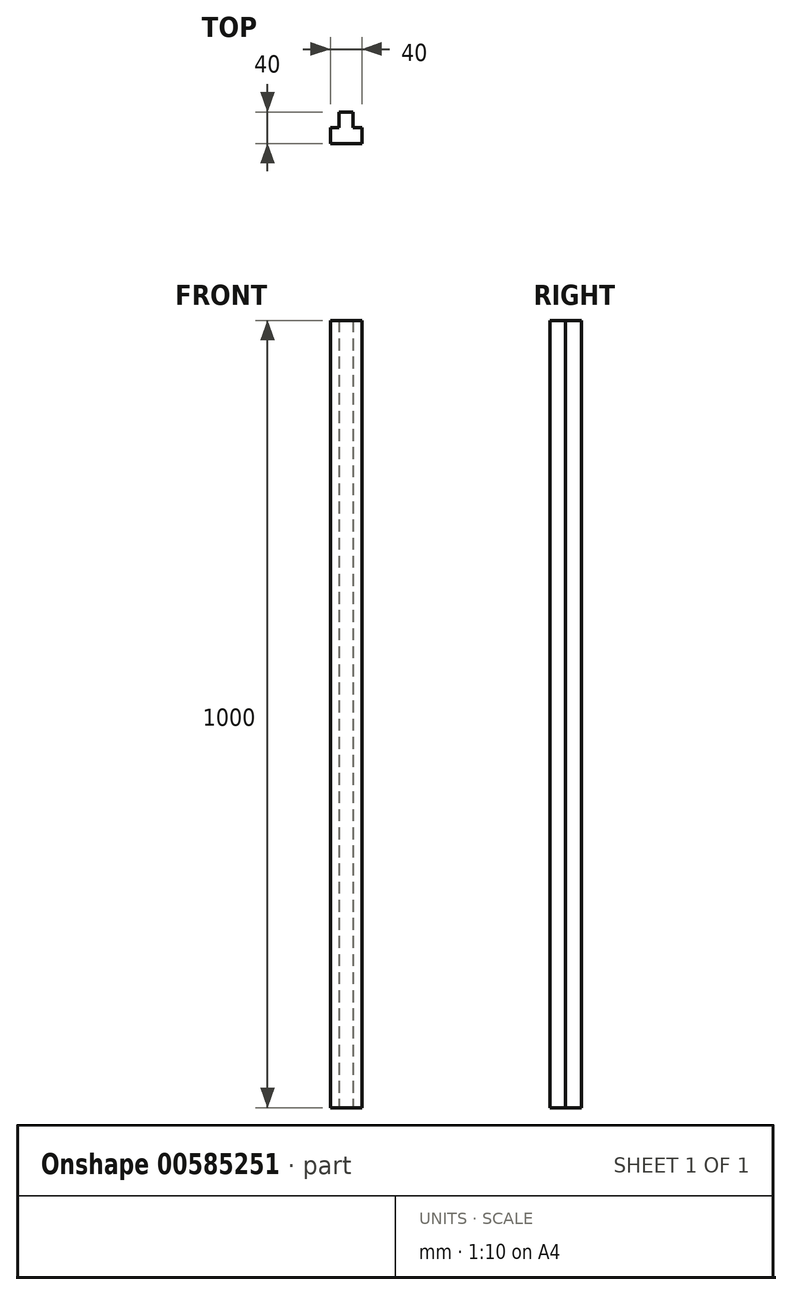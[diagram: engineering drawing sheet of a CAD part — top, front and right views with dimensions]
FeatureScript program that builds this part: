
annotation { "Feature Type Name" : "Feature", "Feature Type Description" : "" }
export const myFeature = defineFeature(function(context is Context, id is Id, definition is map)
    precondition{}
    {
        {
            var Q0;
            Q0=qCreatedBy(makeId("Top.planeOp"),FACE);
            var sketch = newSketch(context, id + "F0", { "sketchPlane" : qUnion([Q0])});
            skLineSegment(sketch, "E0", {"start": v(0, 0) * mm, "end": v(18, 0) * mm});
            skLineSegment(sketch, "E1", {"start": v(18, 0) * mm, "end": v(18, -20) * mm});
            skLineSegment(sketch, "E2", {"start": v(18, -20) * mm, "end": v(29, -20) * mm});
            skLineSegment(sketch, "E3", {"start": v(29, -20) * mm, "end": v(29, -40) * mm});
            skLineSegment(sketch, "E4", {"start": v(29, -40) * mm, "end": v(-11, -40) * mm});
            skLineSegment(sketch, "E5", {"start": v(-11, -40) * mm, "end": v(-11, -20) * mm});
            skLineSegment(sketch, "E6", {"start": v(-11, -20) * mm, "end": v(0, -20) * mm});
            skLineSegment(sketch, "E7", {"start": v(0, -20) * mm, "end": v(0, 0) * mm});
            skSolve(sketch);
        }
        {
            var Q0;
            Q0=makeQuery(id+"F0.imprint","IMPRINT",FACE,{"disambiguationData":[TD([[makeQuery(id+"F0.imprint","IMPRINT",EDGE,{"derivedFrom":sQuery(id+"F0.wireOp",EDGE,"E0")}),-1.0]])]});
            extrude(context, id + "F1", {"entities" : qUnion([Q0]), "depth" : 1000 * mm, "offsetDistance" : 25.4 * mm});
        }
    });
